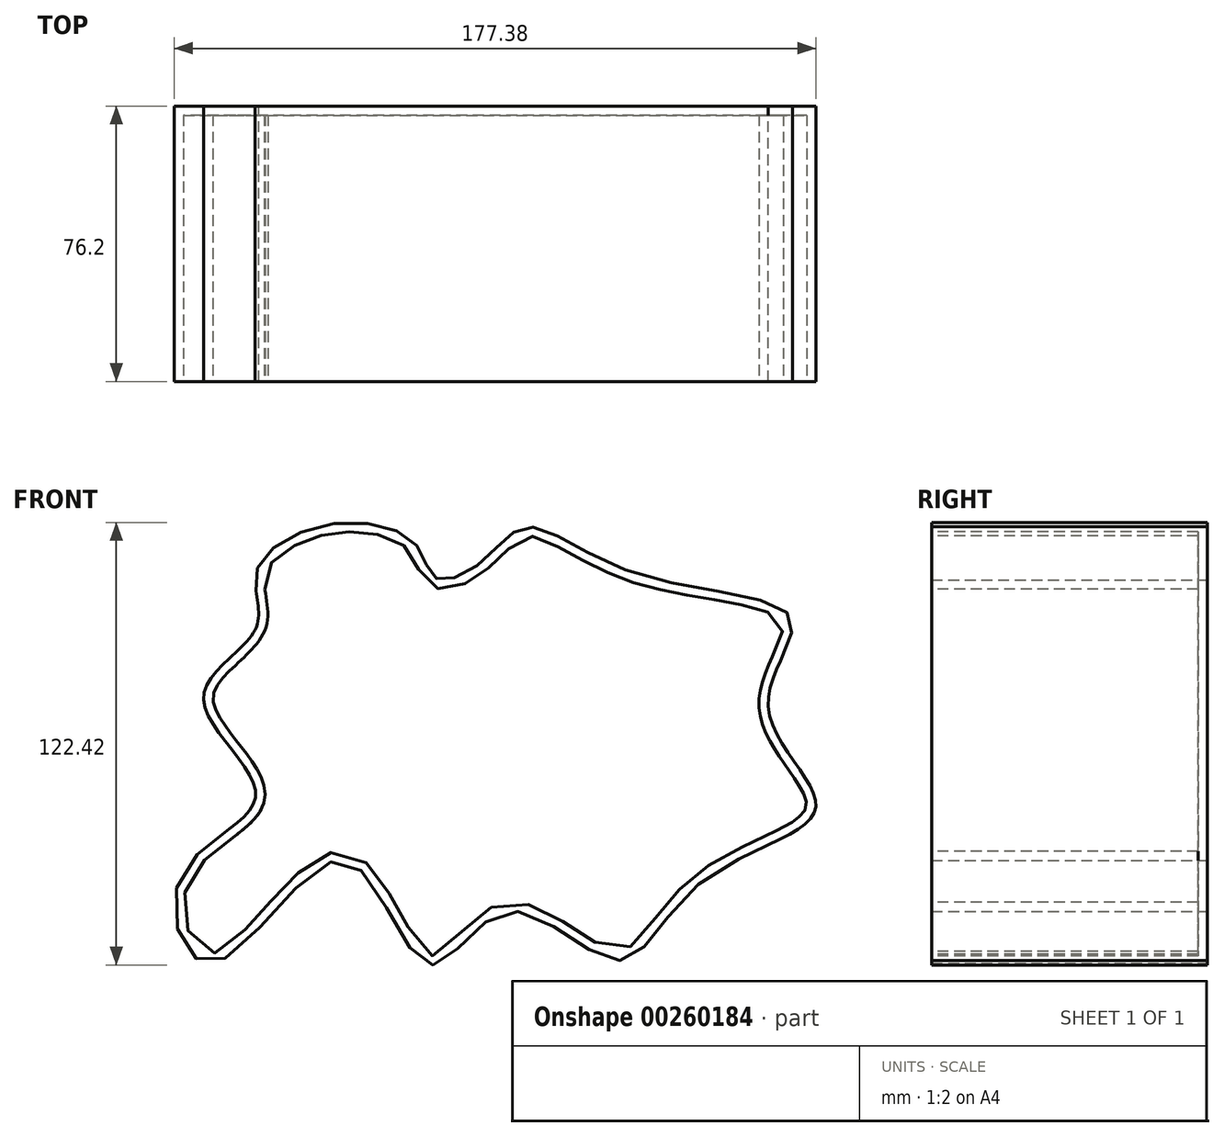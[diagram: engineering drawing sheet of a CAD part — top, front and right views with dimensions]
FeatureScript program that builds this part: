
annotation { "Feature Type Name" : "Feature", "Feature Type Description" : "" }
export const myFeature = defineFeature(function(context is Context, id is Id, definition is map)
    precondition{}
    {
        {
            var Q0;
            Q0=qCreatedBy(makeId("Front.planeOp"),FACE);
            var sketch = newSketch(context, id + "F0", { "sketchPlane" : qUnion([Q0])});
            skLineSegment(sketch, "E0", {"start": v(-76.66, 38.75) * mm, "end": v(-76.66, 37.92) * mm});
            skLineSegment(sketch, "E1", {"start": v(75.74, -12.35) * mm, "end": v(75.74, -12.03) * mm});
            skPoint(sketch, "E2.visualSharp", {"position": v(-76.66, 63.85) * mm});
            skArc(sketch, "E2.filletArc", {"start": v(-69.31, 56.62) * mm, "mid": v(-69.32, 56.61) * mm, "end": v(-69.33, 56.6) * mm});
            skPoint(sketch, "E3.visualSharp", {"position": v(75.74, -37.75) * mm});
            skPoint(sketch, "E4.visualSharp", {"position": v(-76.66, -37.75) * mm});
            skPoint(sketch, "E5.visualSharp", {"position": v(75.73, 65.64) * mm});
            skPoint(sketch, "E6.3.internal.snap0", {"position": v(-69.33, 56.6) * mm});
            skPoint(sketch, "E6.5.internal.snap0", {"position": v(-69.33, 56.6) * mm});
            skFitSpline(sketch, "E6", {"points": [v(-25.12, 69.46) * mm, v(-48.65, 75.06) * mm, v(-69.2, 61.99) * mm, v(-69.33, 46.3) * mm, v(-83.77, 26.88) * mm, v(-69.33, 0) * mm, v(-90.5, -23.18) * mm, v(-81.53, -46.34) * mm, v(-45.3, -17.95) * mm, v(-21.76, -46.71) * mm, v(0, -32.15) * mm, v(30.54, -45.6) * mm, v(53.33, -24.3) * mm, v(85.45, -3.38) * mm, v(72.38, 24.26) * mm, v(78.73, 48.92) * mm, v(35.02, 61.62) * mm, v(5.51, 74.32) * mm, v(-6.78, 64.67) * mm, v(-19.52, 60.12) * mm, v(-25.12, 69.46) * mm]});
            skLineSegment(sketch, "E7.trimOffspring", {"start": v(75.73, 37.34) * mm, "end": v(75.73, 39.94) * mm});
            skLineSegment(sketch, "E8.trimOffspring", {"start": v(-76.66, -9.2) * mm, "end": v(-76.66, -12.35) * mm});
            skSolve(sketch);
        }
        {
            var Q0;
            {var subQ0=sQuery(id+"F0.wireOp",EDGE,"E6");var subQ3=makeQuery(id+"F0.imprint","IMPRINT",VERTEX,{"disambiguationData":[OD(0.0)],"derivedFrom":subQ0});Q0=makeQuery(id+"F0.imprint","IMPRINT",FACE,{"disambiguationData":[TD([[makeQuery(id+"F0.imprint","IMPRINT",EDGE,{"disambiguationData":[TD([[subQ3,1.0]])],"derivedFrom":subQ0}),1.0]])]});}
            extrude(context, id + "F1", {"entities" : qUnion([Q0]), "depth" : 76.2 * mm});
        }
        {
            var Q0;
            Q0=makeQuery(id+"F1.opExtrude","CAP_FACE",FACE,{"disambiguationData":[OSD([sQuery(id+"F0.wireOp",EDGE,"E6")])],"isStart":false});
            shell(context, id + "F2", {"entities" : qUnion([Q0]), "thickness" : 2.54 * mm});
        }
    });
